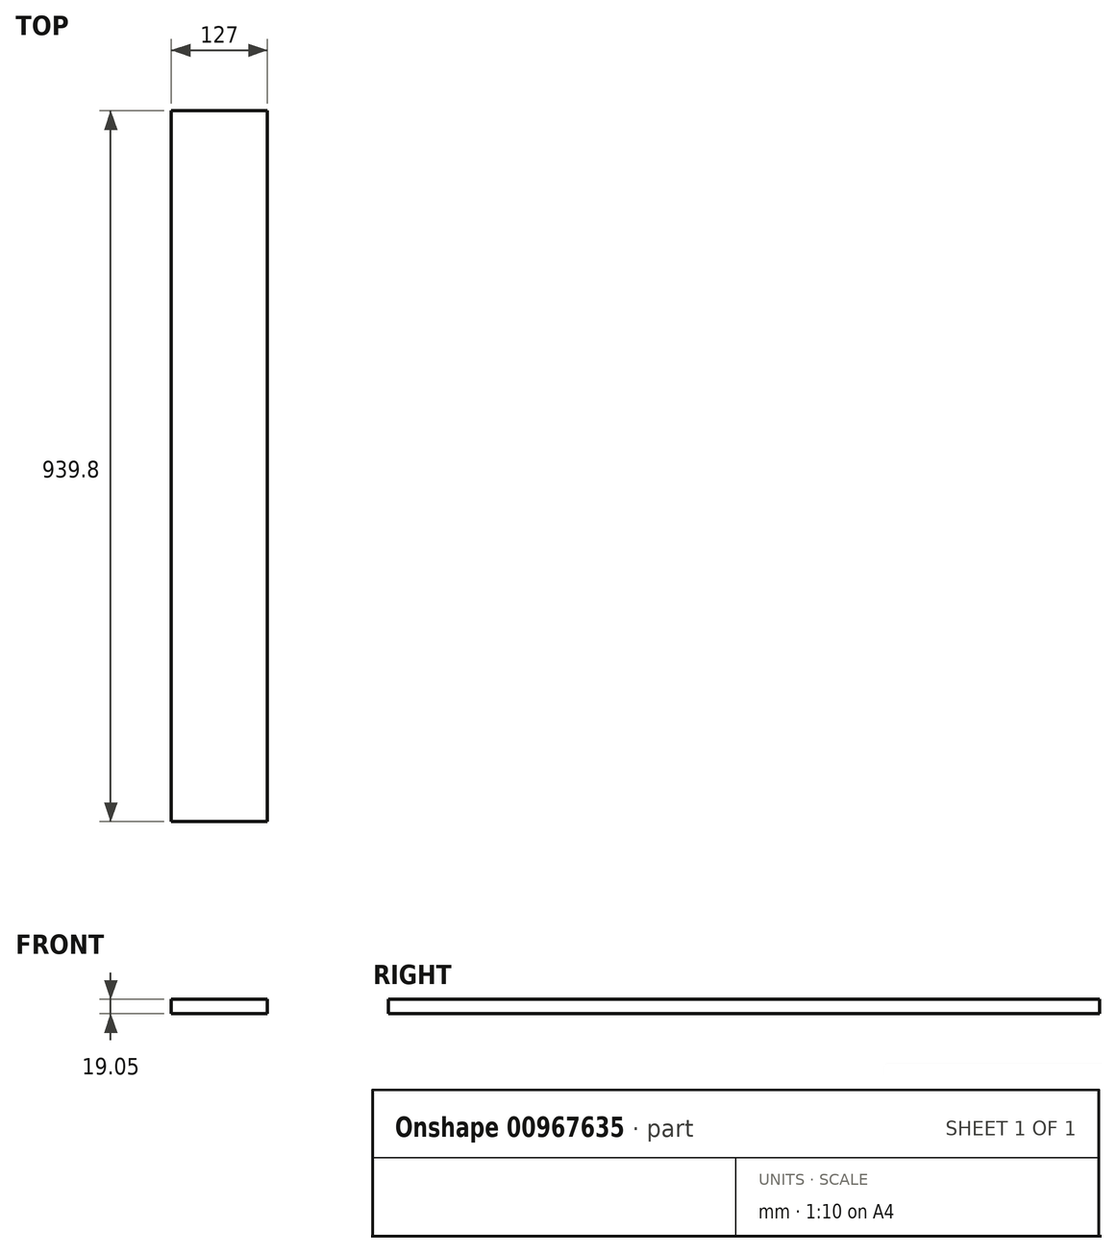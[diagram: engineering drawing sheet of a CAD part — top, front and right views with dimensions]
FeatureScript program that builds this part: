
annotation { "Feature Type Name" : "Feature", "Feature Type Description" : "" }
export const myFeature = defineFeature(function(context is Context, id is Id, definition is map)
    precondition{}
    {
        {
            var Q0;
            Q0=qCreatedBy(makeId("Top.planeOp"),FACE);
            var sketch = newSketch(context, id + "F0", { "sketchPlane" : qUnion([Q0])});
            skLineSegment(sketch, "E0.bottom", {"start": v(0, 0) * mm, "end": v(127, 0) * mm});
            skLineSegment(sketch, "E0.top", {"start": v(0, 939.8) * mm, "end": v(127, 939.8) * mm});
            skLineSegment(sketch, "E0.left", {"start": v(0, 0) * mm, "end": v(0, 939.8) * mm});
            skLineSegment(sketch, "E0.right", {"start": v(127, 0) * mm, "end": v(127, 939.8) * mm});
            skSolve(sketch);
        }
        {
            var Q0;
            Q0 = qSketchRegion(id + "F0", true);
            extrude(context, id + "F1", {"entities" : qUnion([Q0]), "depth" : 19.05 * mm, "offsetDistance" : 25.4 * mm});
        }
    });
